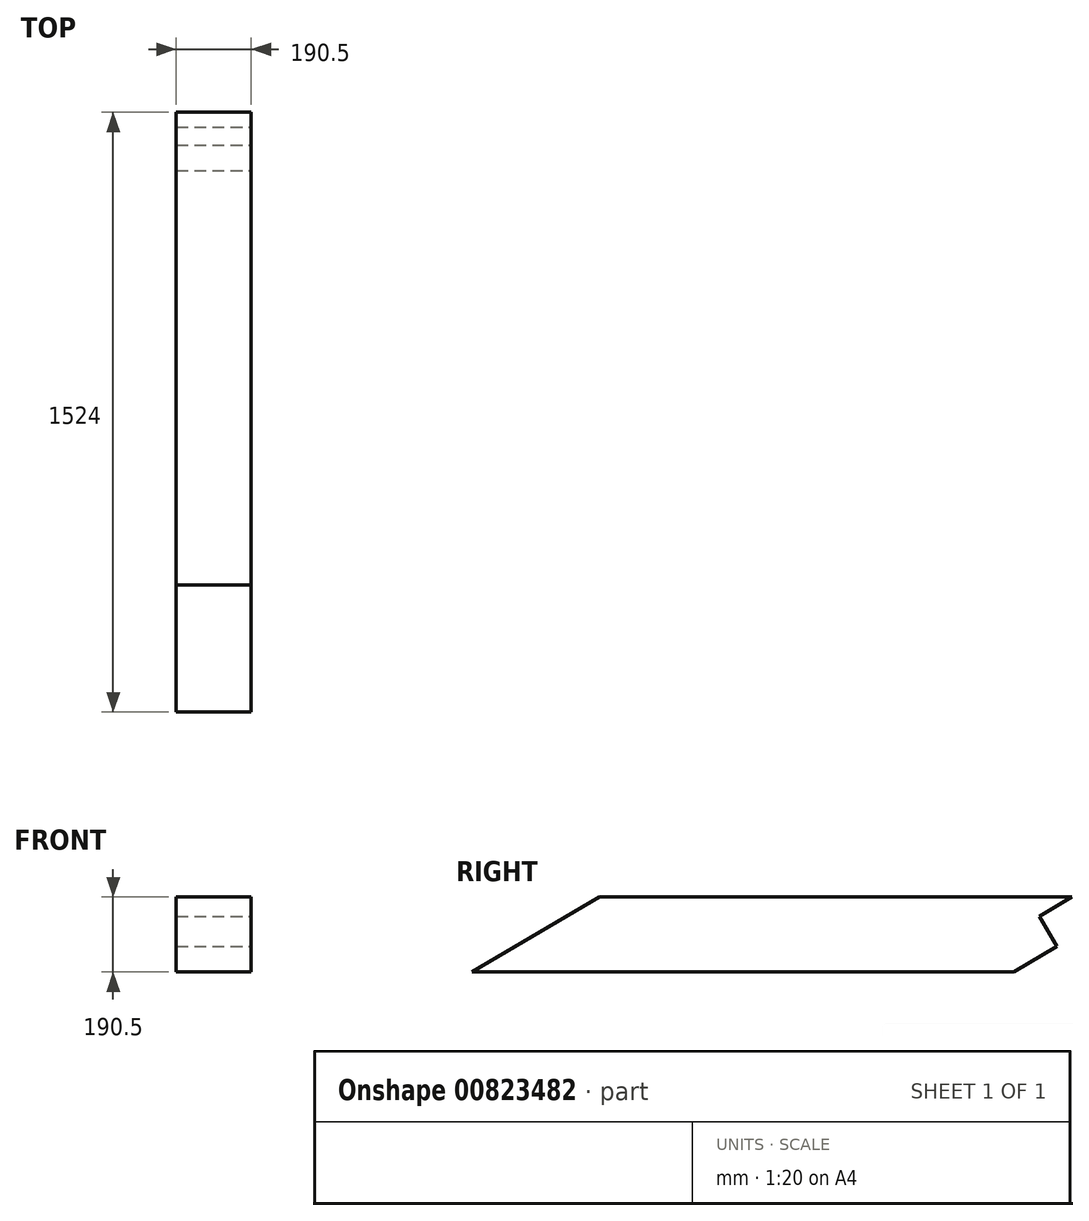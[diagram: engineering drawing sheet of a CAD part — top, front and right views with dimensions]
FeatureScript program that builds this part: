
annotation { "Feature Type Name" : "Feature", "Feature Type Description" : "" }
export const myFeature = defineFeature(function(context is Context, id is Id, definition is map)
    precondition{}
    {
        {
            var Q0;
            Q0=qCreatedBy(makeId("Front.planeOp"),FACE);
            var sketch = newSketch(context, id + "F0", { "sketchPlane" : qUnion([Q0])});
            skLineSegment(sketch, "E0.bottom", {"start": v(0, 0) * mm, "end": v(190.5, 0) * mm});
            skLineSegment(sketch, "E0.top", {"start": v(0, 190.5) * mm, "end": v(190.5, 190.5) * mm});
            skLineSegment(sketch, "E0.left", {"start": v(0, 0) * mm, "end": v(0, 190.5) * mm});
            skLineSegment(sketch, "E0.right", {"start": v(190.5, 0) * mm, "end": v(190.5, 190.5) * mm});
            skSolve(sketch);
        }
        {
            var Q0;
            Q0 = qSketchRegion(id + "F0", true);
            extrude(context, id + "F1", {"entities" : qUnion([Q0]), "depth" : 1524 * mm, "offsetDistance" : 25.4 * mm});
        }
        {
            var Q0;
            Q0=makeQuery(id+"F1.opExtrude","SWEPT_FACE",FACE,{"disambiguationData":[OSD([sQuery(id+"F0.wireOp",EDGE,"E0.right")])]});
            var sketch = newSketch(context, id + "F2", { "sketchPlane" : qUnion([Q0])});
            skLineSegment(sketch, "E1", {"start": v(-1524, 0) * mm, "end": v(-1200.73, 190.5) * mm});
            skLineSegment(sketch, "E2", {"start": v(-1200.73, 190.5) * mm, "end": v(-1524, 190.5) * mm});
            skLineSegment(sketch, "E3", {"start": v(-1524, 190.5) * mm, "end": v(-1524, 0) * mm});
            skLineSegment(sketch, "E4", {"start": v(0, 0) * mm, "end": v(-83.32, 141.4) * mm});
            skLineSegment(sketch, "E5", {"start": v(-83.32, 141.4) * mm, "end": v(0, 190.5) * mm});
            skLineSegment(sketch, "E6", {"start": v(0, 190.5) * mm, "end": v(0, 0) * mm});
            skSolve(sketch);
        }
        {
            var Q0;
            Q0 = qSketchRegion(id + "F2", true);
            extrude(context, id + "F3", {"entities" : qUnion([Q0]), "operationType" : NewBodyOperationType.REMOVE, "endBound" : BoundingType.THROUGH_ALL, "oppositeDirection" : true, "depth" : 25.4 * mm, "offsetDistance" : 25.4 * mm});
        }
        {
            var Q0;
            Q0=makeQuery(id+"F1.opExtrude","SWEPT_FACE",FACE,{"disambiguationData":[OSD([sQuery(id+"F0.wireOp",EDGE,"E0.right")])]});
            var sketch = newSketch(context, id + "F4", { "sketchPlane" : qUnion([Q0])});
            skLineSegment(sketch, "E7", {"start": v(-38.2, 64.8) * mm, "end": v(-148.17, 0) * mm});
            skLineSegment(sketch, "E8", {"start": v(-148.17, 0) * mm, "end": v(0, 0) * mm});
            skLineSegment(sketch, "E9", {"start": v(0, 0) * mm, "end": v(-38.2, 64.8) * mm});
            skSolve(sketch);
        }
        {
            var Q0;
            Q0 = qSketchRegion(id + "F4", true);
            extrude(context, id + "F5", {"entities" : qUnion([Q0]), "operationType" : NewBodyOperationType.REMOVE, "endBound" : BoundingType.THROUGH_ALL, "oppositeDirection" : true, "depth" : 25.4 * mm, "offsetDistance" : 25.4 * mm});
        }
    });
